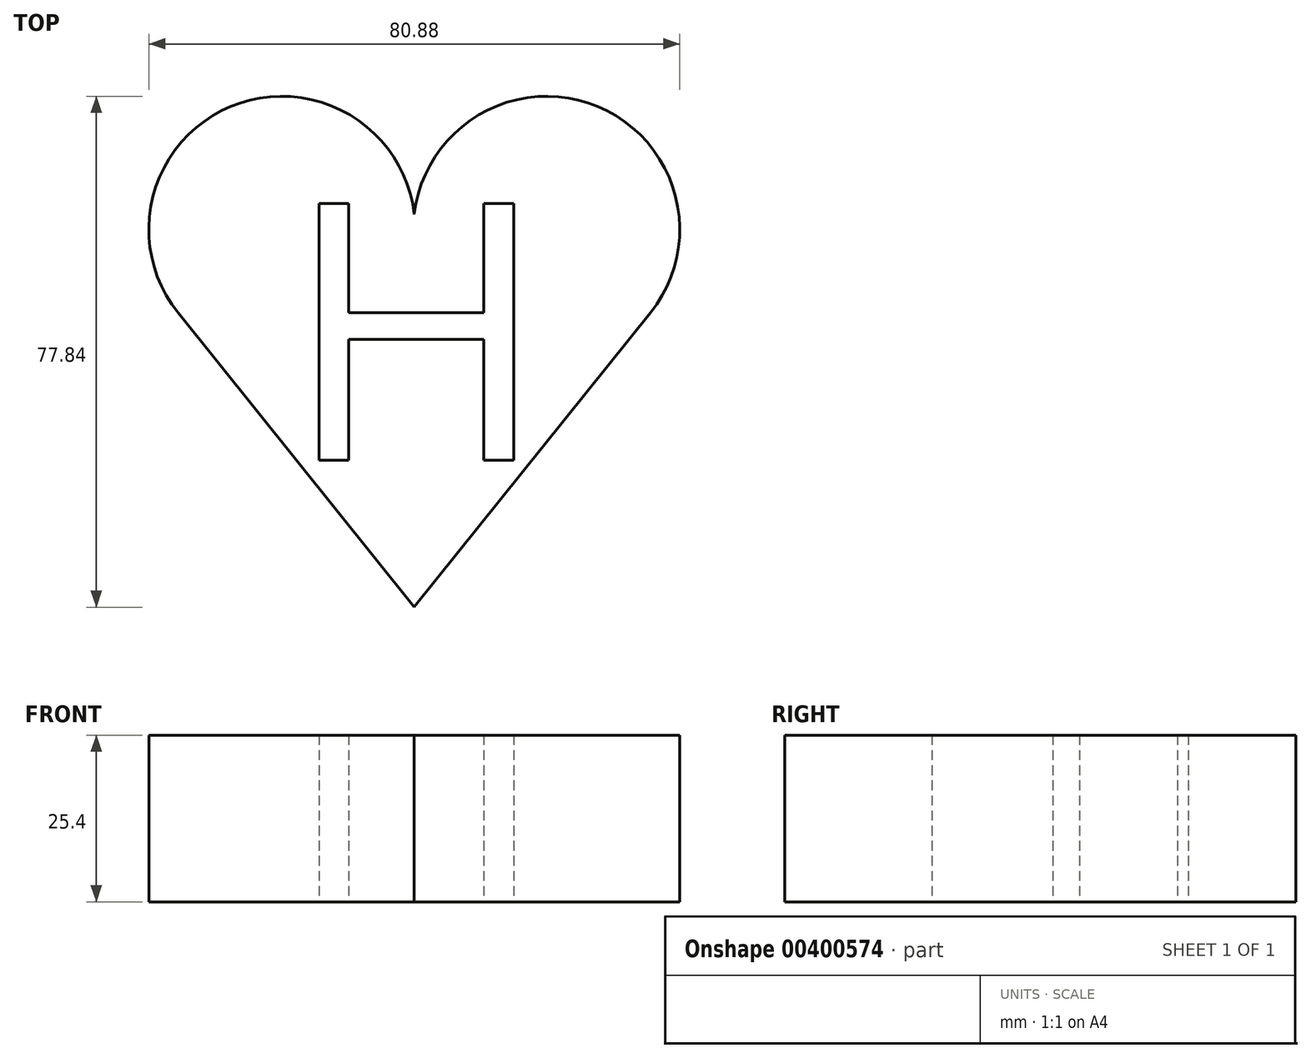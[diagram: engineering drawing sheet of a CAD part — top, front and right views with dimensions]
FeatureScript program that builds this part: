
annotation { "Feature Type Name" : "Feature", "Feature Type Description" : "" }
export const myFeature = defineFeature(function(context is Context, id is Id, definition is map)
    precondition{}
    {
        {
            var Q0;
            Q0=qCreatedBy(makeId("Top.planeOp"),FACE);
            var sketch = newSketch(context, id + "F0", { "sketchPlane" : qUnion([Q0])});
            skText(sketch, "E0", { "text": "H\n", "fontName": "OpenSans-Regular.ttf"});
            const initialGuessF0  = {"E0": [-0.0332, -0.02275, 1, 0, 0.0394]};
            skSetInitialGuess(sketch, initialGuessF0);
            skSolve(sketch);
        }
        {
            var Q0;
            Q0=makeQuery(id+"F0.imprint","IMPRINT",FACE,{"disambiguationData":[TD([[makeQuery(id+"F0.imprint","IMPRINT",EDGE,{"derivedFrom":sQuery(id+"F0.wireOp",EDGE,"E0.sketch_text.stroke-0")}),-1.0]])]});
            extrude(context, id + "F1", {"entities" : qUnion([Q0]), "depth" : 25.4 * mm});
        }
        {
            var Q0;
            Q0=qCreatedBy(makeId("Top.planeOp"),FACE);
            var sketch = newSketch(context, id + "F2", { "sketchPlane" : qUnion([Q0])});
            skLineSegment(sketch, "E1", {"start": v(-54.2, -8.47) * mm, "end": v(-54.2, -68.78) * mm, "construction": true});
            skLineSegment(sketch, "E2", {"start": v(-54.2, -68.78) * mm, "end": v(-18.22, -23.92) * mm});
            skArc(sketch, "E3", {"start": v(-18.22, -23.92) * mm, "mid": v(-26.25, 7.5) * mm, "end": v(-54.2, -8.96) * mm});
            skArc(sketch, "E4.MirrorCS", {"start": v(-90.17, -23.92) * mm, "mid": v(-82.13, 7.5) * mm, "end": v(-54.2, -8.96) * mm});
            skLineSegment(sketch, "E5.MirrorCS", {"start": v(-54.2, -68.78) * mm, "end": v(-90.17, -23.92) * mm});
            skSolve(sketch);
        }
        {
            var Q0;
            Q0=makeQuery(id+"F2.imprint","IMPRINT",FACE,{"disambiguationData":[TD([[makeQuery(id+"F2.imprint","IMPRINT",EDGE,{"derivedFrom":sQuery(id+"F2.wireOp",EDGE,"E2")}),1.0]])]});
            extrude(context, id + "F3", {"entities" : qUnion([Q0]), "depth" : 25.4 * mm});
        }
        {
            var Q0;
            Q0=makeQuery(id+"F3.opExtrude","SWEPT_BODY",BODY,{"disambiguationData":[OSD([sQuery(id+"F2.wireOp",EDGE,"E2"),sQuery(id+"F2.wireOp",EDGE,"E3"),sQuery(id+"F2.wireOp",EDGE,"E4.MirrorCS"),sQuery(id+"F2.wireOp",EDGE,"E5.MirrorCS")])]});
            transform(context, id + "F4", {"entities" : qUnion([Q0]), "transformType" : TransformType.TRANSLATION_3D, "dx" : 40.9 * mm, "dy" : 23.62 * mm, "dz" : 0 * mm, "makeCopy" : false});
        }
    });
